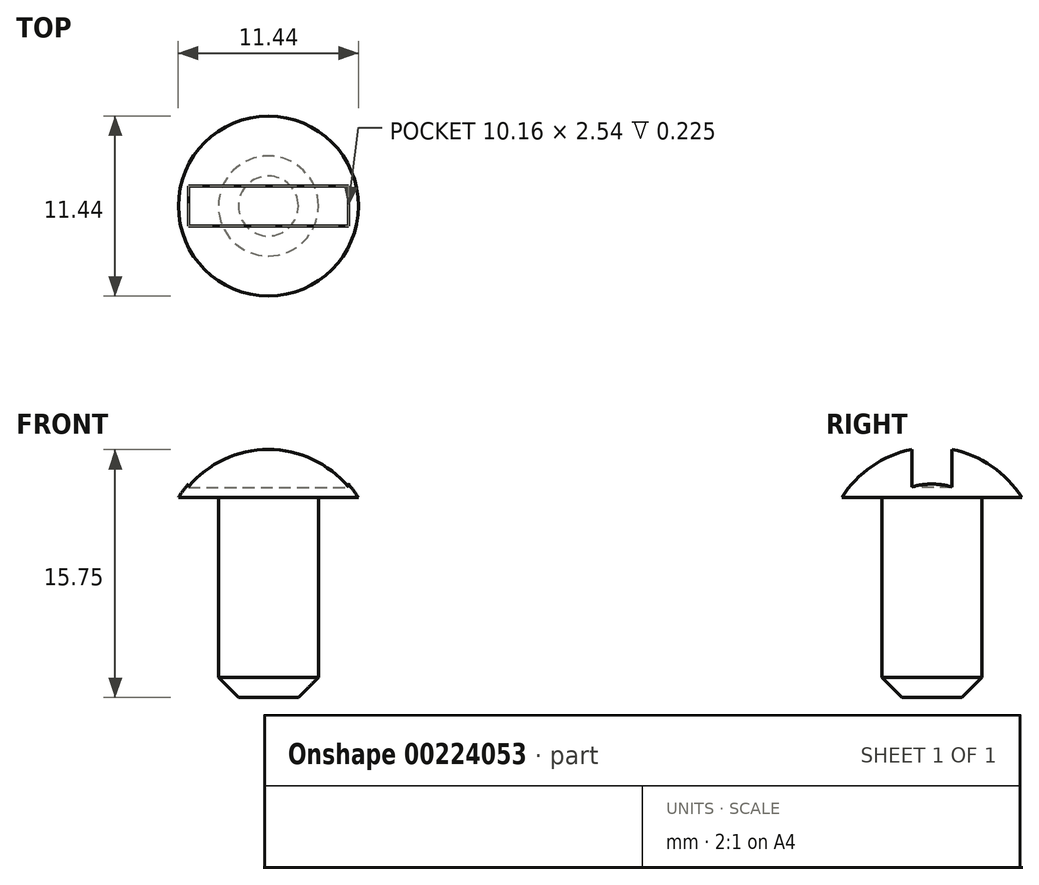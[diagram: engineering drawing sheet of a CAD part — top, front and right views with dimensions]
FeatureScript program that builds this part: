
annotation { "Feature Type Name" : "Feature", "Feature Type Description" : "" }
export const myFeature = defineFeature(function(context is Context, id is Id, definition is map)
    precondition{}
    {
        {
            var Q0;
            Q0=qCreatedBy(makeId("Front.planeOp"),FACE);
            var sketch = newSketch(context, id + "F0", { "sketchPlane" : qUnion([Q0])});
            skLineSegment(sketch, "E0", {"start": v(0, 0) * mm, "end": v(3.18, 0) * mm});
            skLineSegment(sketch, "E1", {"start": v(3.18, 0) * mm, "end": v(3.18, 12.7) * mm});
            skLineSegment(sketch, "E2", {"start": v(3.18, 12.7) * mm, "end": v(5.71, 12.7) * mm});
            skLineSegment(sketch, "E3", {"start": v(0, 0) * mm, "end": v(0, 15.87) * mm});
            skArc(sketch, "E4", {"start": v(5.72, 12.7) * mm, "mid": v(3.27, 15.03) * mm, "end": v(0, 15.87) * mm});
            skLineSegment(sketch, "E5", {"start": v(0, 15.87) * mm, "end": v(0, -2.84) * mm, "construction": true});
            skSolve(sketch);
        }
        {
            var Q0;
            Q0=makeQuery(id+"F0.imprint","IMPRINT",FACE,{"disambiguationData":[TD([[makeQuery(id+"F0.imprint","IMPRINT",EDGE,{"derivedFrom":sQuery(id+"F0.wireOp",EDGE,"E0")}),1.0]])]});
            var Q1;
            Q1=sQuery(id+"F0.wireOp",EDGE,"E5");
            revolve(context, id + "F1", {"entities" : qUnion([Q0]), "axis" : qUnion([Q1]), "revolveType" : RevolveType.FULL});
        }
        {
            var Q0;
            Q0=makeQuery(id+"F1.opRevolve","SWEPT_FACE",FACE,{"disambiguationData":[OSD([sQuery(id+"F0.wireOp",EDGE,"E2")])]});
            cPlane(context, id + "F2", {"entities" : qUnion([Q0]), "cplaneType" : CPlaneType.OFFSET, "offset" : 0.64 * mm, "oppositeDirection" : true, "width" : 152.4 * mm, "height" : 152.4 * mm});
        }
        {
            var Q0;
            Q0=qCreatedBy(id+"F2.planeOp",FACE);
            var sketch = newSketch(context, id + "F3", { "sketchPlane" : qUnion([Q0])});
            skLineSegment(sketch, "E6.bottom", {"start": v(-5.08, -1.27) * mm, "end": v(5.08, -1.27) * mm});
            skLineSegment(sketch, "E6.top", {"start": v(-5.08, 1.27) * mm, "end": v(5.08, 1.27) * mm});
            skLineSegment(sketch, "E6.left", {"start": v(-5.08, -1.27) * mm, "end": v(-5.08, 1.27) * mm});
            skLineSegment(sketch, "E6.right", {"start": v(5.08, -1.27) * mm, "end": v(5.08, 1.27) * mm});
            skPoint(sketch, "E6.middle", {"position": v(0, 0) * mm});
            skSolve(sketch);
        }
        {
            var Q0;
            Q0 = qSketchRegion(id + "F3", true);
            extrude(context, id + "F4", {"entities" : qUnion([Q0]), "operationType" : NewBodyOperationType.REMOVE, "endBound" : BoundingType.THROUGH_ALL, "oppositeDirection" : true, "depth" : 25.4 * mm});
        }
        {
            var Q0;
            Q0=makeQuery(id+"F1.opRevolve","SWEPT_EDGE",EDGE,{"disambiguationData":[OSD([sQuery(id+"F0.wireOp",EDGE,"E0"),sQuery(id+"F0.wireOp",EDGE,"E1")])]});
            chamfer(context, id + "F5", {"entities" : qUnion([Q0]), "width" : 1.27 * mm, "tangentPropagation" : true});
        }
    });
